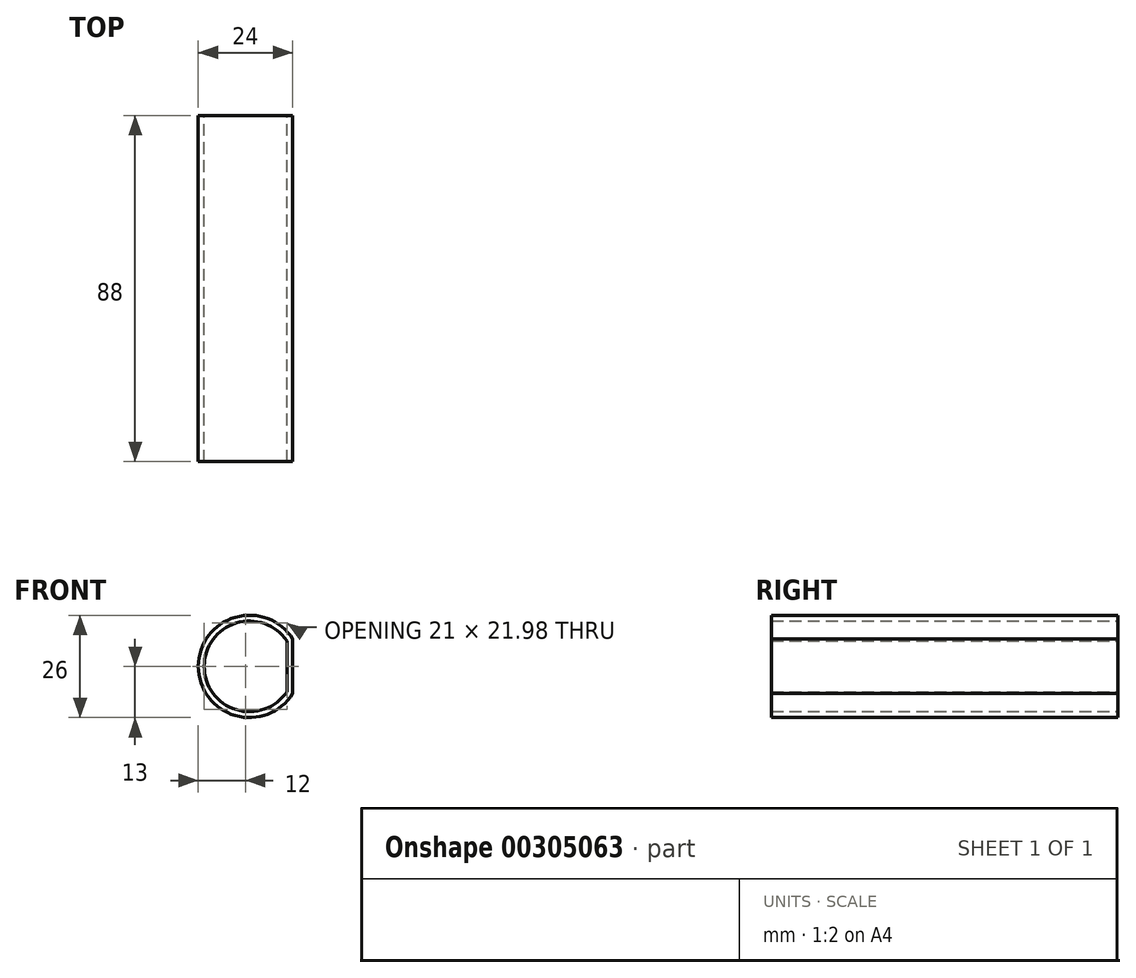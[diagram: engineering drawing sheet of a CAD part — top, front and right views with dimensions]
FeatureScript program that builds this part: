
annotation { "Feature Type Name" : "Feature", "Feature Type Description" : "" }
export const myFeature = defineFeature(function(context is Context, id is Id, definition is map)
    precondition{}
    {
        {
            var Q0;
            Q0=qCreatedBy(makeId("Front.planeOp"),FACE);
            var sketch = newSketch(context, id + "F0", { "sketchPlane" : qUnion([Q0])});
            skArc(sketch, "E0", {"start": v(11, 6.93) * mm, "mid": v(-13, 0) * mm, "end": v(11, -6.93) * mm});
            skLineSegment(sketch, "E1", {"start": v(11, 6.93) * mm, "end": v(11, -6.93) * mm});
            skPoint(sketch, "E2", {"position": v(-12.84, 2.05) * mm});
            skArc(sketch, "E3.0", {"start": v(9.5, 6.48) * mm, "mid": v(-11.5, 0) * mm, "end": v(9.5, -6.48) * mm});
            skLineSegment(sketch, "E3.1", {"start": v(9.5, 6.48) * mm, "end": v(9.5, -6.48) * mm});
            skSolve(sketch);
        }
        {
            var Q0;
            Q0=makeQuery(id+"F0.imprint","IMPRINT",FACE,{"disambiguationData":[TD([[makeQuery(id+"F0.imprint","IMPRINT",EDGE,{"derivedFrom":sQuery(id+"F0.wireOp",EDGE,"E0")}),1.0]])]});
            extrude(context, id + "F1", {"entities" : qUnion([Q0]), "depth" : 88 * mm});
        }
    });
